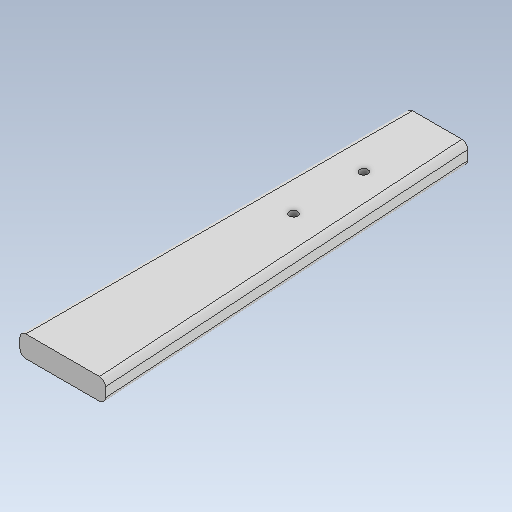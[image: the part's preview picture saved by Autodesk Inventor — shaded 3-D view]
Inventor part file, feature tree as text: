
AUTODESK INVENTOR PART (.ipt)
format: ipt  version: 2020 (Build 240168000, 168)  size: 93,696 bytes
history: native  units: mm
features: other x3, sketch x2
ambient origin geometry x8: Origin, YZ Plane, XZ Plane, XY Plane, X Axis, Y Axis, Z Axis, Center Point
bodies: Volumenkörper1 (feature_tree)
feature tree (5):
  other  "Brillenbuegel.ipt"
  other  "Volumenkörper1::Brillenbuegel.ipt"
  other  "Bezeichnung1"
  sketch  "Skizze1"  dims[d0=10.0mm]
  sketch  "Skizze2"
